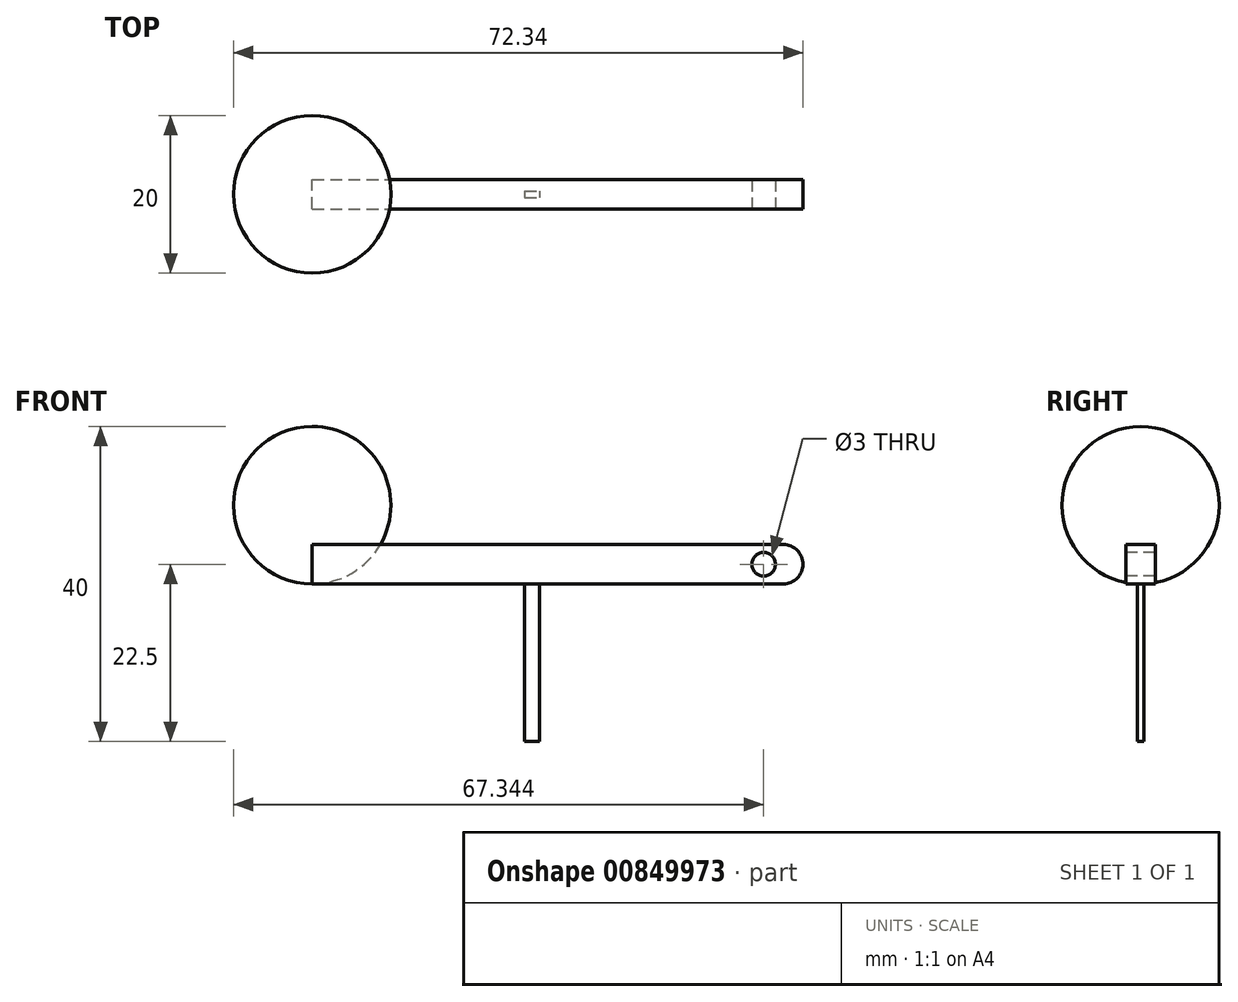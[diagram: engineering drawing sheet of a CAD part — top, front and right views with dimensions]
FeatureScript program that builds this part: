
annotation { "Feature Type Name" : "Feature", "Feature Type Description" : "" }
export const myFeature = defineFeature(function(context is Context, id is Id, definition is map)
    precondition{}
    {
        {
            var Q0;
            Q0=qCreatedBy(makeId("Top.planeOp"),FACE);
            var sketch = newSketch(context, id + "F0", { "sketchPlane" : qUnion([Q0])});
            skCircle(sketch, "E0", {"center": v(0, 0) * mm, "radius": 10 * mm});
            skSolve(sketch);
        }
        {
            var Q0;
            Q0=makeQuery(id+"F0.imprint","IMPRINT",FACE,{"disambiguationData":[TD([[makeQuery(id+"F0.imprint","IMPRINT",EDGE,{"derivedFrom":sQuery(id+"F0.wireOp",EDGE,"E0")}),1.0]])]});
            extrude(context, id + "F1", {"entities" : qUnion([Q0]), "depth" : 20 * mm, "offsetDistance" : 25 * mm});
        }
        {
            var Q0;
            Q0=makeQuery(id+"F1.opExtrude","CAP_EDGE",EDGE,{"disambiguationData":[OSD([sQuery(id+"F0.wireOp",EDGE,"E0")])],"isStart":false});
            var Q1;
            Q1=makeQuery(id+"F1.opExtrude","CAP_EDGE",EDGE,{"disambiguationData":[OSD([sQuery(id+"F0.wireOp",EDGE,"E0")])],"isStart":true});
            fillet(context, id + "F2", {"entities" : qUnion([Q0, Q1]), "radius" : 10 * mm, "tangentPropagation" : true, "allowEdgeOverflow" : false});
        }
        {
            var Q0;
            Q0=qCreatedBy(makeId("Top.planeOp"),FACE);
            var sketch = newSketch(context, id + "F3", { "sketchPlane" : qUnion([Q0])});
            skLineSegment(sketch, "E1.bottom", {"start": v(0, -1.86) * mm, "end": v(62.34, -1.86) * mm});
            skLineSegment(sketch, "E1.top", {"start": v(0, 1.86) * mm, "end": v(62.34, 1.86) * mm});
            skLineSegment(sketch, "E1.left", {"start": v(0, -1.86) * mm, "end": v(0, 1.86) * mm});
            skLineSegment(sketch, "E1.right", {"start": v(62.34, -1.86) * mm, "end": v(62.34, 1.86) * mm});
            skPoint(sketch, "E1.middle", {"position": v(31.17, 0) * mm});
            skSolve(sketch);
        }
        {
            var Q0;
            Q0=makeQuery(id+"F3.imprint","IMPRINT",FACE,{"disambiguationData":[TD([[makeQuery(id+"F3.imprint","IMPRINT",EDGE,{"derivedFrom":sQuery(id+"F3.wireOp",EDGE,"E1.bottom")}),1.0]])]});
            extrude(context, id + "F4", {"entities" : qUnion([Q0]), "depth" : 5 * mm, "offsetDistance" : 25 * mm});
        }
        {
            var Q0;
            Q0=makeQuery(id+"F4.opExtrude","SWEPT_FACE",FACE,{"disambiguationData":[OSD([sQuery(id+"F3.wireOp",EDGE,"E1.bottom")])]});
            var sketch = newSketch(context, id + "F5", { "sketchPlane" : qUnion([Q0])});
            skCircle(sketch, "E2", {"center": v(57.34, 2.5) * mm, "radius": 1.5 * mm});
            skSolve(sketch);
        }
        {
            var Q0;
            Q0=makeQuery(id+"F5.imprint","IMPRINT",FACE,{"disambiguationData":[TD([[makeQuery(id+"F5.imprint","IMPRINT",EDGE,{"derivedFrom":sQuery(id+"F5.wireOp",EDGE,"E2")}),1.0]])]});
            extrude(context, id + "F6", {"entities" : qUnion([Q0]), "operationType" : NewBodyOperationType.REMOVE, "oppositeDirection" : true, "depth" : 25 * mm, "offsetDistance" : 25 * mm});
        }
        {
            var Q0;
            Q0=makeQuery(id+"F4.opExtrude","CAP_EDGE",EDGE,{"disambiguationData":[OSD([sQuery(id+"F3.wireOp",EDGE,"E1.right")])],"isStart":true});
            var Q1;
            Q1=makeQuery(id+"F4.opExtrude","CAP_EDGE",EDGE,{"disambiguationData":[OSD([sQuery(id+"F3.wireOp",EDGE,"E1.right")])],"isStart":false});
            fillet(context, id + "F7", {"entities" : qUnion([Q0, Q1]), "radius" : 2.5 * mm, "tangentPropagation" : true, "allowEdgeOverflow" : false});
        }
        {
            var Q0;
            Q0=makeQuery(id+"F4.opExtrude","CAP_FACE",FACE,{"disambiguationData":[OSD([sQuery(id+"F3.wireOp",EDGE,"E1.bottom"),sQuery(id+"F3.wireOp",EDGE,"E1.top"),sQuery(id+"F3.wireOp",EDGE,"E1.left"),sQuery(id+"F3.wireOp",EDGE,"E1.right")])],"isStart":true});
            var sketch = newSketch(context, id + "F8", { "sketchPlane" : qUnion([Q0])});
            skLineSegment(sketch, "E3.bottom", {"start": v(27, -0.42) * mm, "end": v(28.86, -0.42) * mm});
            skLineSegment(sketch, "E3.top", {"start": v(27, 0.42) * mm, "end": v(28.86, 0.42) * mm});
            skLineSegment(sketch, "E3.left", {"start": v(27, -0.42) * mm, "end": v(27, 0.42) * mm});
            skLineSegment(sketch, "E3.right", {"start": v(28.86, -0.42) * mm, "end": v(28.86, 0.42) * mm});
            skPoint(sketch, "E3.middle", {"position": v(27.93, 0) * mm});
            skSolve(sketch);
        }
        {
            var Q0;
            Q0=makeQuery(id+"F8.imprint","IMPRINT",FACE,{"disambiguationData":[TD([[makeQuery(id+"F8.imprint","IMPRINT",EDGE,{"derivedFrom":sQuery(id+"F8.wireOp",EDGE,"E3.bottom")}),1.0]])]});
            extrude(context, id + "F9", {"entities" : qUnion([Q0]), "operationType" : NewBodyOperationType.ADD, "depth" : 20 * mm, "offsetDistance" : 25 * mm});
        }
    });
